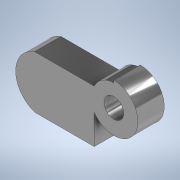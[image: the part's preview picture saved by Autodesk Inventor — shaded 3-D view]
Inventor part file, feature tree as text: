
AUTODESK INVENTOR PART (.ipt)
format: ipt  version: 2021 (Build 250183000, 183)  size: 135,168 bytes
history: native  units: in
note: dims shown in document units (in); Inventor stores cm internally (conversion verified against a paired STEP export)
features: extrude x4, sketch x4, projected_geometry x1
ambient origin geometry x8: Origin, YZ Plane, XZ Plane, XY Plane, X Axis, Y Axis, Z Axis, Center Point
bodies: Solid1 (feature_tree)
feature tree (9):
  extrude  "Extrusion1"  Depth=0.0787in TaperAngle=0.0deg
  extrude  "Extrusion2"  TaperAngle=0.0deg  [1 undecoded]
  extrude  "Extrusion3"  Depth=0.0079in
  extrude  "Extrusion6"  Depth=0.0787in TaperAngle=0.0deg
  sketch  "Sketch1"  dims[d0=0.1433in d1=0.0787in d2=0.0in]
  sketch  "Sketch2"  dims[d3=0.0591in d4=0.0in d5=0.0in]
  sketch  "Sketch3"  dims[d6=0.0448in d7=0.0079in]
  sketch  "Sketch5"  dims[d8=0.0in d9=0.0in d16=0.0787in d17=0.0in d18=0.1772in d10=0.1969in d11=0.0344in]
  projected_geometry  "Projected Loop2"
note: 1 required parameter value undecoded (feature->parameter linkage not recoverable at this tier; creation-order binding heuristic only, values carry confidence <= 0.55)
